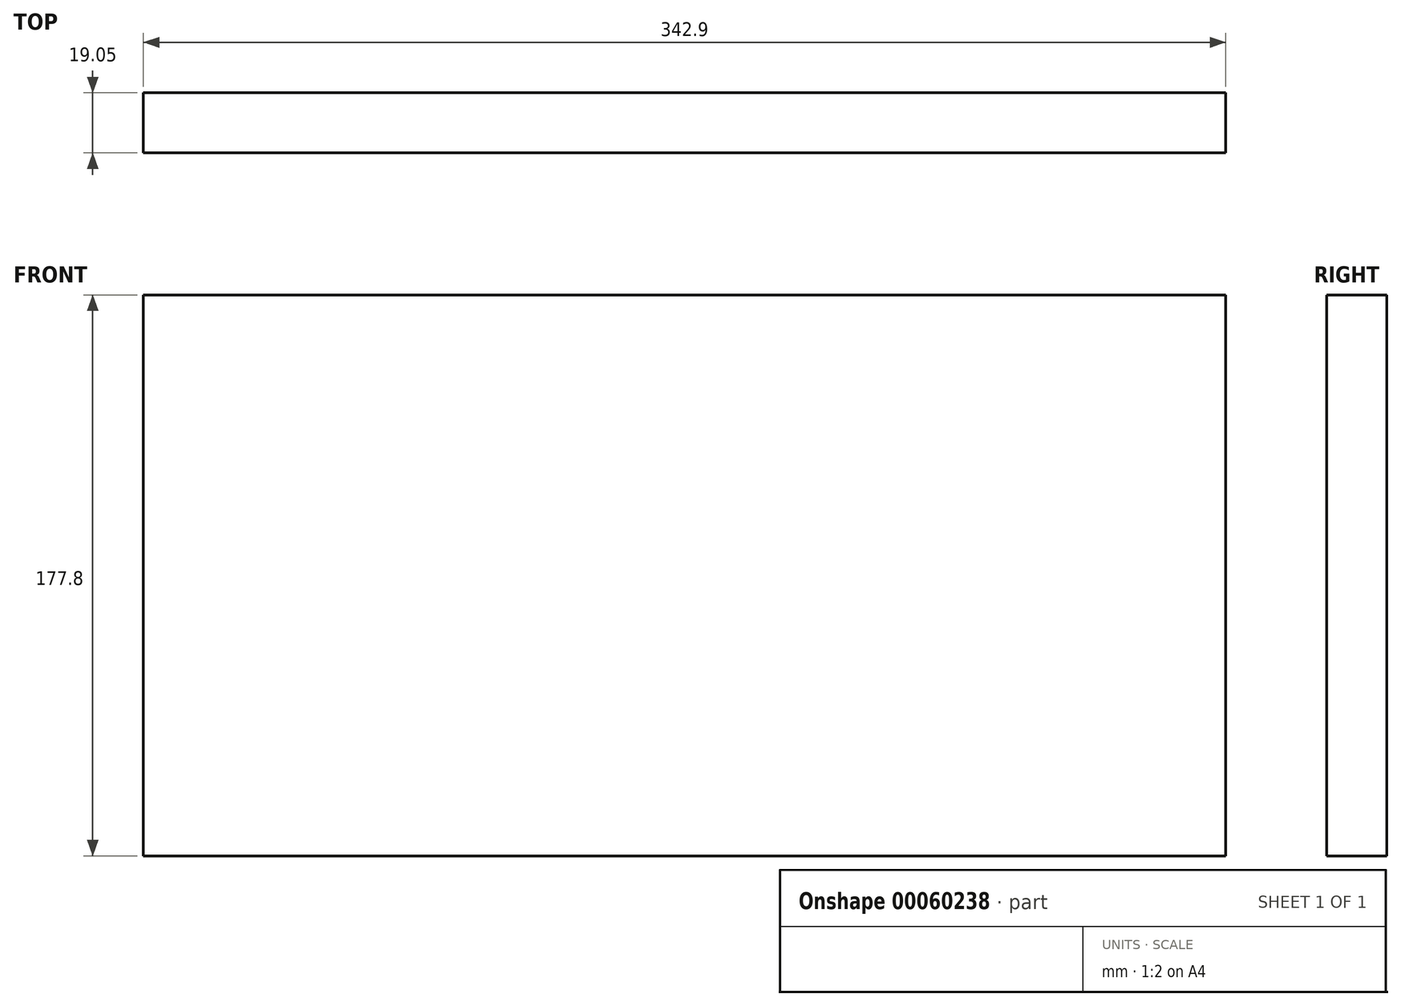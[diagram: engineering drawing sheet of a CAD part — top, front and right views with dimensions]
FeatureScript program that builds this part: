
annotation { "Feature Type Name" : "Feature", "Feature Type Description" : "" }
export const myFeature = defineFeature(function(context is Context, id is Id, definition is map)
    precondition{}
    {
        {
            var Q0;
            Q0=qCreatedBy(makeId("Front.planeOp"),FACE);
            var sketch = newSketch(context, id + "F0", { "sketchPlane" : qUnion([Q0])});
            skLineSegment(sketch, "E0.rect.bottom", {"start": v(171.45, -88.9) * mm, "end": v(-171.45, -88.9) * mm});
            skLineSegment(sketch, "E0.rect.top", {"start": v(171.45, 88.9) * mm, "end": v(-171.45, 88.9) * mm});
            skLineSegment(sketch, "E0.rect.left", {"start": v(171.45, -88.9) * mm, "end": v(171.45, 88.9) * mm});
            skLineSegment(sketch, "E0.rect.right", {"start": v(-171.45, -88.9) * mm, "end": v(-171.45, 88.9) * mm});
            skPoint(sketch, "E0.rect.middle", {"position": v(0, 0) * mm});
            skSolve(sketch);
        }
        {
            var Q0;
            Q0 = qSketchRegion(id + "F0", true);
            extrude(context, id + "F1", {"entities" : qUnion([Q0]), "depth" : 19.05 * mm});
        }
    });
